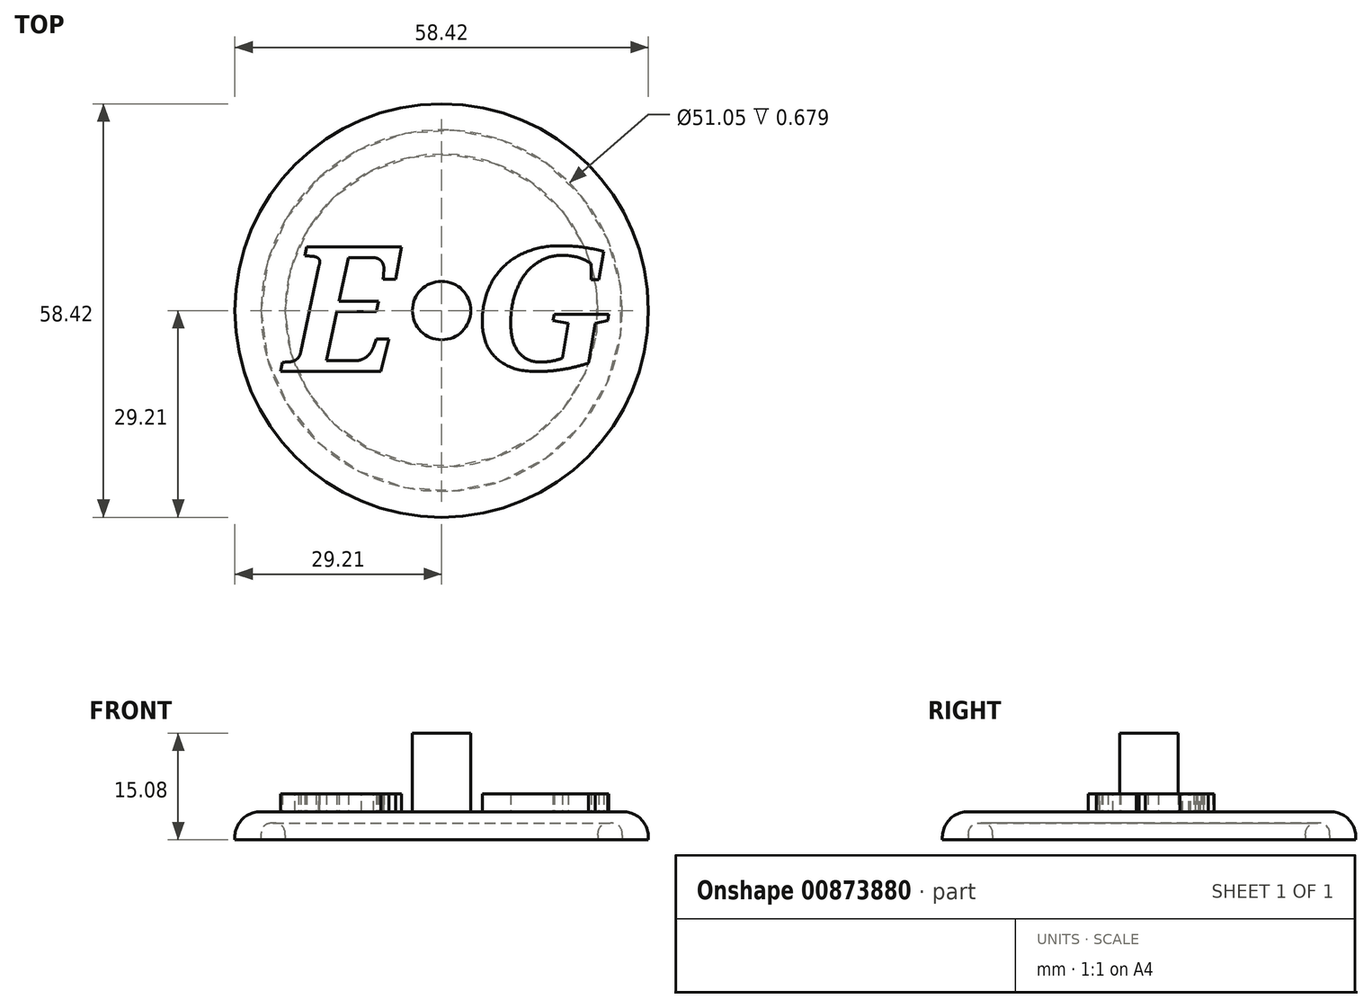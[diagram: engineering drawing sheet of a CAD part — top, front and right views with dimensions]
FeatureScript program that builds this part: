
annotation { "Feature Type Name" : "Feature", "Feature Type Description" : "" }
export const myFeature = defineFeature(function(context is Context, id is Id, definition is map)
    precondition{}
    {
        {
            var Q0;
            Q0=qCreatedBy(makeId("Top.planeOp"),FACE);
            var sketch = newSketch(context, id + "F0", { "sketchPlane" : qUnion([Q0])});
            skCircle(sketch, "E0", {"center": v(0, 0) * mm, "radius": 29.21 * mm});
            skSolve(sketch);
        }
        {
            var Q0;
            Q0=makeQuery(id+"F0.imprint","IMPRINT",FACE,{"disambiguationData":[TD([[makeQuery(id+"F0.imprint","IMPRINT",EDGE,{"derivedFrom":sQuery(id+"F0.wireOp",EDGE,"E0")}),1.0]])]});
            extrude(context, id + "F1", {"entities" : qUnion([Q0]), "depth" : 3.97 * mm, "offsetDistance" : 25.4 * mm});
        }
        {
            var Q0;
            Q0=makeQuery(id+"F1.opExtrude","CAP_FACE",FACE,{"disambiguationData":[OSD([sQuery(id+"F0.wireOp",EDGE,"E0")])],"isStart":true});
            var sketch = newSketch(context, id + "F2", { "sketchPlane" : qUnion([Q0])});
            skCircle(sketch, "E1", {"center": v(0, 0) * mm, "radius": 22.1 * mm});
            skCircle(sketch, "E2", {"center": v(0, 0) * mm, "radius": 25.53 * mm});
            skSolve(sketch);
        }
        {
            var Q0;
            Q0=makeQuery(id+"F2.imprint","IMPRINT",FACE,{"disambiguationData":[TD([[makeQuery(id+"F2.imprint","IMPRINT",EDGE,{"derivedFrom":sQuery(id+"F2.wireOp",EDGE,"E1")}),-1.0]])]});
            extrude(context, id + "F3", {"entities" : qUnion([Q0]), "operationType" : NewBodyOperationType.REMOVE, "oppositeDirection" : true, "depth" : 2.38 * mm, "offsetDistance" : 25.4 * mm});
        }
        {
            var Q0;
            Q0=makeQuery(id+"F1.opExtrude","CAP_FACE",FACE,{"disambiguationData":[OSD([sQuery(id+"F0.wireOp",EDGE,"E0")])],"isStart":false});
            fillet(context, id + "F4", {"entities" : qUnion([Q0]), "radius" : 3.56 * mm, "tangentPropagation" : true, "allowEdgeOverflow" : false});
        }
        {
            var Q0;
            Q0=makeQuery(id+"F3.boolean.opBoolean","COPY",FACE,{"derivedFrom":makeQuery(id+"F3.opExtrude","CAP_FACE",FACE,{"disambiguationData":[OSD([sQuery(id+"F2.wireOp",EDGE,"E1"),sQuery(id+"F2.wireOp",EDGE,"E2")])],"isStart":false})});
            fillet(context, id + "F5", {"entities" : qUnion([Q0]), "radius" : 1.7 * mm, "tangentPropagation" : true, "rho" : 0.5, "crossSection" : FilletCrossSection.CONIC, "allowEdgeOverflow" : false});
        }
        {
            var Q0;
            Q0=makeQuery(id+"F1.opExtrude","CAP_FACE",FACE,{"disambiguationData":[OSD([sQuery(id+"F0.wireOp",EDGE,"E0")])],"isStart":false});
            var sketch = newSketch(context, id + "F6", { "sketchPlane" : qUnion([Q0])});
            skCircle(sketch, "E3", {"center": v(0, 0) * mm, "radius": 4.13 * mm});
            skSolve(sketch);
        }
        {
            var Q0;
            Q0=makeQuery(id+"F6.imprint","IMPRINT",FACE,{"disambiguationData":[TD([[makeQuery(id+"F6.imprint","IMPRINT",EDGE,{"derivedFrom":sQuery(id+"F6.wireOp",EDGE,"E3")}),1.0]])]});
            extrude(context, id + "F7", {"entities" : qUnion([Q0]), "operationType" : NewBodyOperationType.ADD, "depth" : 11.1 * mm, "offsetDistance" : 25.4 * mm});
        }
        {
            var Q0;
            Q0=makeQuery(id+"F1.opExtrude","CAP_FACE",FACE,{"disambiguationData":[OSD([sQuery(id+"F0.wireOp",EDGE,"E0")])],"isStart":false});
            var sketch = newSketch(context, id + "F8", { "sketchPlane" : qUnion([Q0])});
            skText(sketch, "E4", { "text": "G", "fontName": "Tinos-BoldItalic.ttf"});
            const initialGuessF8  = {"E4": [0.00484, -0.00835, 1, 0, 0.01903]};
            skSetInitialGuess(sketch, initialGuessF8);
            skSolve(sketch);
        }
        {
            var Q0;
            Q0=makeQuery(id+"F8.imprint","IMPRINT",FACE,{"disambiguationData":[TD([[makeQuery(id+"F8.imprint","IMPRINT",EDGE,{"derivedFrom":sQuery(id+"F8.wireOp",EDGE,"E4.sketch_text.stroke-0")}),-1.0]])]});
            extrude(context, id + "F9", {"entities" : qUnion([Q0]), "operationType" : NewBodyOperationType.ADD, "depth" : 2.54 * mm, "offsetDistance" : 25.4 * mm});
        }
        {
            var Q0;
            Q0=makeQuery(id+"F1.opExtrude","CAP_FACE",FACE,{"disambiguationData":[OSD([sQuery(id+"F0.wireOp",EDGE,"E0")])],"isStart":false});
            var sketch = newSketch(context, id + "F10", { "sketchPlane" : qUnion([Q0])});
            skText(sketch, "E5", { "text": "E", "fontName": "NotoSerif-BoldItalic.ttf"});
            const initialGuessF10  = {"E5": [-0.02218, -0.00861, 1, 0, 0.01776]};
            skSetInitialGuess(sketch, initialGuessF10);
            skSolve(sketch);
        }
        {
            var Q0;
            Q0=makeQuery(id+"F10.imprint","IMPRINT",FACE,{"disambiguationData":[TD([[makeQuery(id+"F10.imprint","IMPRINT",EDGE,{"derivedFrom":sQuery(id+"F10.wireOp",EDGE,"E5.sketch_text.stroke-0")}),-1.0]])]});
            extrude(context, id + "F11", {"entities" : qUnion([Q0]), "operationType" : NewBodyOperationType.ADD, "depth" : 2.54 * mm, "offsetDistance" : 25.4 * mm});
        }
    });
